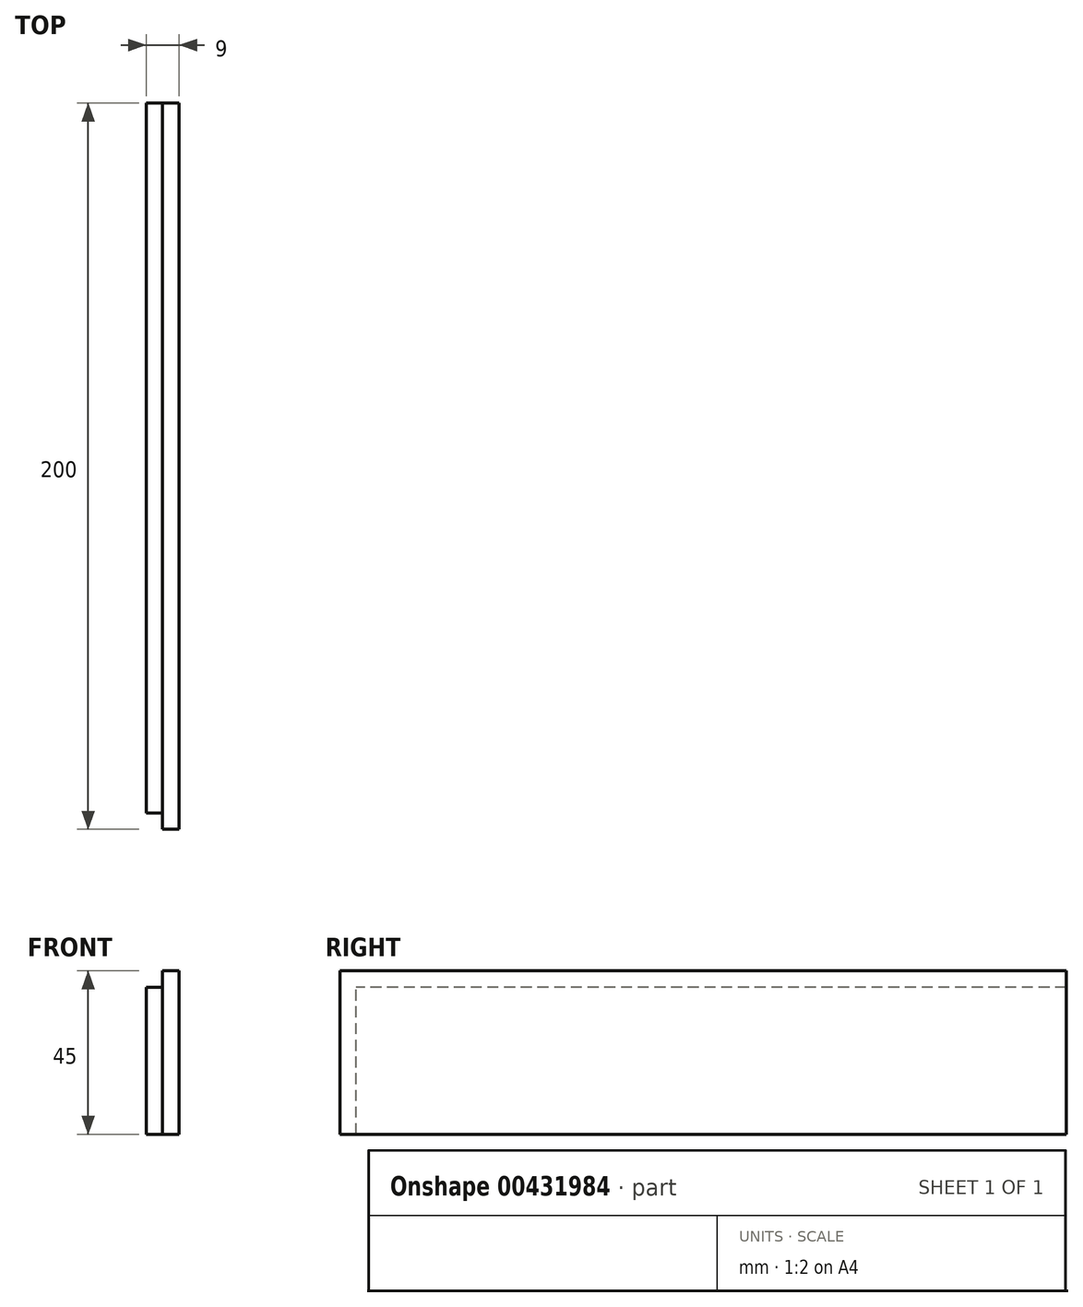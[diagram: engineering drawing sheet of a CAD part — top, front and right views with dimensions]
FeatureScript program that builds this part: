
annotation { "Feature Type Name" : "Feature", "Feature Type Description" : "" }
export const myFeature = defineFeature(function(context is Context, id is Id, definition is map)
    precondition{}
    {
        {
            var Q0;
            Q0=qCreatedBy(makeId("Right.planeOp"),FACE);
            var sketch = newSketch(context, id + "F0", { "sketchPlane" : qUnion([Q0])});
            skLineSegment(sketch, "E0.bottom", {"start": v(100, 22.5) * mm, "end": v(-100, 22.5) * mm});
            skLineSegment(sketch, "E0.top", {"start": v(100, -22.5) * mm, "end": v(-100, -22.5) * mm});
            skLineSegment(sketch, "E0.left", {"start": v(100, 22.5) * mm, "end": v(100, -22.5) * mm});
            skLineSegment(sketch, "E0.right", {"start": v(-100, 22.5) * mm, "end": v(-100, -22.5) * mm});
            skPoint(sketch, "E0.middle", {"position": v(0, 0) * mm});
            skSolve(sketch);
        }
        {
            var Q0;
            Q0 = qSketchRegion(id + "F0", true);
            extrude(context, id + "F1", {"entities" : qUnion([Q0]), "depth" : 9 * mm, "offsetDistance" : 25 * mm});
        }
        {
            var Q0;
            Q0=makeQuery(id+"F1.opExtrude","SWEPT_FACE",FACE,{"disambiguationData":[OSD([sQuery(id+"F0.wireOp",EDGE,"E0.right")])]});
            var sketch = newSketch(context, id + "F2", { "sketchPlane" : qUnion([Q0])});
            skLineSegment(sketch, "E1.bottom", {"start": v(0, 22.5) * mm, "end": v(4.5, 22.5) * mm});
            skLineSegment(sketch, "E1.top", {"start": v(0, 18) * mm, "end": v(4.5, 18) * mm});
            skLineSegment(sketch, "E1.left", {"start": v(0, 22.5) * mm, "end": v(0, 18) * mm});
            skLineSegment(sketch, "E1.right", {"start": v(4.5, 22.5) * mm, "end": v(4.5, 18) * mm});
            skSolve(sketch);
        }
        {
            var Q0;
            Q0=qSketchRegion(id+"F2",true);
            extrude(context, id + "F3", {"entities" : qUnion([Q0]), "operationType" : NewBodyOperationType.REMOVE, "endBound" : BoundingType.THROUGH_ALL, "oppositeDirection" : true, "depth" : 25 * mm});
        }
        {
            var Q0;
            Q0=makeQuery(id+"F3.boolean.opBoolean","COPY",FACE,{"derivedFrom":makeQuery(id+"F3.opExtrude","SWEPT_FACE",FACE,{"disambiguationData":[OSD([sQuery(id+"F2.wireOp",EDGE,"E1.top")])]})});
            var sketch = newSketch(context, id + "F4", { "sketchPlane" : qUnion([Q0])});
            skLineSegment(sketch, "E2.bottom", {"start": v(0, -100) * mm, "end": v(4.5, -100) * mm});
            skLineSegment(sketch, "E2.top", {"start": v(0, -95.5) * mm, "end": v(4.5, -95.5) * mm});
            skLineSegment(sketch, "E2.left", {"start": v(0, -100) * mm, "end": v(0, -95.5) * mm});
            skLineSegment(sketch, "E2.right", {"start": v(4.5, -100) * mm, "end": v(4.5, -95.5) * mm});
            skSolve(sketch);
        }
        {
            var Q0;
            Q0=qSketchRegion(id+"F4",true);
            extrude(context, id + "F5", {"entities" : qUnion([Q0]), "operationType" : NewBodyOperationType.REMOVE, "endBound" : BoundingType.THROUGH_ALL, "oppositeDirection" : true, "depth" : 25 * mm});
        }
    });
